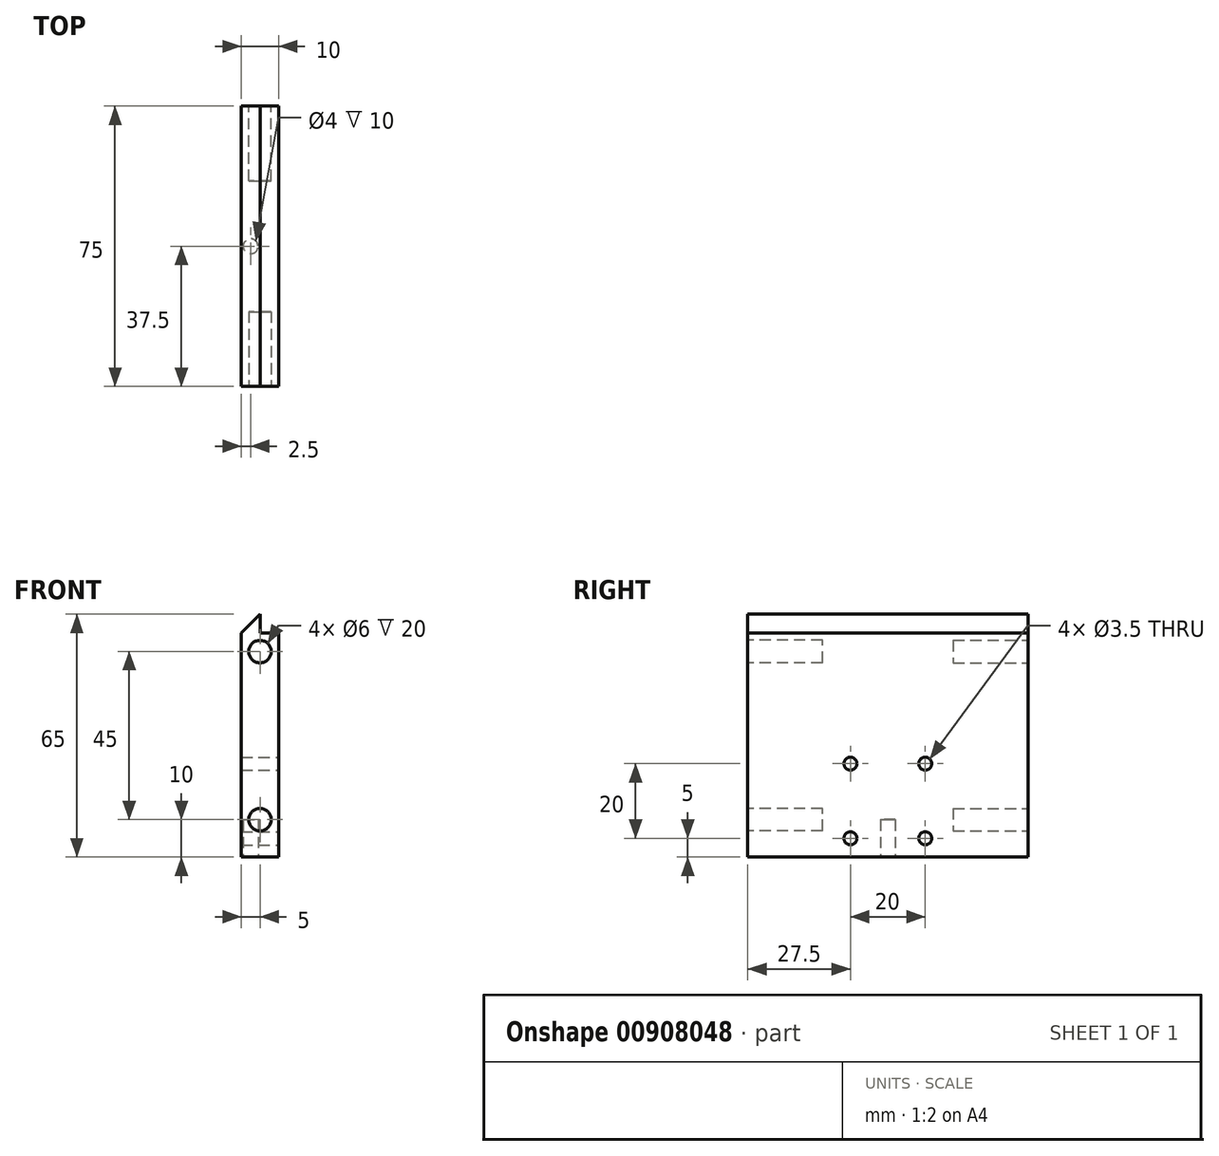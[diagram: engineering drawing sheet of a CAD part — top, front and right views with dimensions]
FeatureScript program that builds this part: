
annotation { "Feature Type Name" : "Feature", "Feature Type Description" : "" }
export const myFeature = defineFeature(function(context is Context, id is Id, definition is map)
    precondition{}
    {
        {
            var Q0;
            Q0=qCreatedBy(makeId("Front.planeOp"),FACE);
            var sketch = newSketch(context, id + "F0", { "sketchPlane" : qUnion([Q0])});
            skLineSegment(sketch, "E0.top", {"start": v(-5, -32.5) * mm, "end": v(5, -32.5) * mm});
            skLineSegment(sketch, "E0.left", {"start": v(-5, 27.5) * mm, "end": v(-5, -32.5) * mm});
            skLineSegment(sketch, "E0.right", {"start": v(5, 27.5) * mm, "end": v(5, -32.5) * mm});
            skPoint(sketch, "E0.middle", {"position": v(0, 0) * mm});
            skPoint(sketch, "E1", {"position": v(0, -22.5) * mm});
            skPoint(sketch, "E2", {"position": v(0, 22.5) * mm});
            skLineSegment(sketch, "E3", {"start": v(0, 32.5) * mm, "end": v(-5, 27.5) * mm});
            skLineSegment(sketch, "E4.top", {"start": v(0, 27.5) * mm, "end": v(5, 27.5) * mm});
            skLineSegment(sketch, "E4.left", {"start": v(0, 32.5) * mm, "end": v(0, 27.5) * mm});
            skSolve(sketch);
        }
        {
            var Q0;
            {var subQ1=sQuery(id+"F0.wireOp",EDGE,"E0.top");Q0=makeQuery(id+"F0.imprint","IMPRINT",FACE,{"disambiguationData":[TD([[makeQuery(id+"F0.imprint","IMPRINT",EDGE,{"derivedFrom":subQ1}),1.0]])]});}
            extrude(context, id + "F1", {"entities" : qUnion([Q0]), "depth" : 75 * mm, "offsetDistance" : 25 * mm});
        }
        {
            var Q0;
            Q0=makeQuery(id+"F1.opExtrude","SWEPT_FACE",FACE,{"disambiguationData":[OSD([sQuery(id+"F0.wireOp",EDGE,"E0.top")])]});
            var sketch = newSketch(context, id + "F2", { "sketchPlane" : qUnion([Q0])});
            skPoint(sketch, "E5.centerSnap0", {"position": v(-5, 37.5) * mm});
            skCircle(sketch, "E6", {"center": v(-2.5, 37.5) * mm, "radius": 2 * mm});
            skSolve(sketch);
        }
        {
            var Q0;
            Q0=makeQuery(id+"F1.opExtrude","SWEPT_FACE",FACE,{"disambiguationData":[OSD([sQuery(id+"F0.wireOp",EDGE,"E0.right")])]});
            var sketch = newSketch(context, id + "F3", { "sketchPlane" : qUnion([Q0])});
            skCircle(sketch, "E7", {"center": v(-27.5, -7.5) * mm, "radius": 1.75 * mm});
            skCircle(sketch, "E8", {"center": v(-47.5, -7.5) * mm, "radius": 1.75 * mm});
            skCircle(sketch, "E9", {"center": v(-27.5, -27.5) * mm, "radius": 1.75 * mm});
            skCircle(sketch, "E10", {"center": v(-47.5, -27.5) * mm, "radius": 1.75 * mm});
            skSolve(sketch);
        }
        {
            var Q0;
            Q0=qSketchRegion(id+"F3",true);
            extrude(context, id + "F4", {"entities" : qUnion([Q0]), "operationType" : NewBodyOperationType.REMOVE, "oppositeDirection" : true, "depth" : 25 * mm, "offsetDistance" : 25 * mm});
        }
        {
            var Q0;
            Q0=makeQuery(id+"F1.opExtrude","SWEPT_FACE",FACE,{"disambiguationData":[OSD([sQuery(id+"F0.wireOp",EDGE,"E0.top")])]});
            var sketch = newSketch(context, id + "F5", { "sketchPlane" : qUnion([Q0])});
            skSolve(sketch);
        }
        {
            var Q0;
            Q0=makeQuery(id+"F1.opExtrude","CAP_FACE",FACE,{"disambiguationData":[OSD([sQuery(id+"F0.wireOp",EDGE,"E0.top"),sQuery(id+"F0.wireOp",EDGE,"E0.left"),sQuery(id+"F0.wireOp",EDGE,"E0.right"),sQuery(id+"F0.wireOp",EDGE,"E3"),sQuery(id+"F0.wireOp",EDGE,"E4.top"),sQuery(id+"F0.wireOp",EDGE,"E4.left")])],"isStart":false});
            var sketch = newSketch(context, id + "F6", { "sketchPlane" : qUnion([Q0])});
            skCircle(sketch, "E11", {"center": v(0, -22.5) * mm, "radius": 3 * mm});
            skPoint(sketch, "E11.centerSnap0", {"position": v(0, -32.5) * mm});
            skSolve(sketch);
        }
        {
            var Q0;
            Q0=qSketchRegion(id+"F6",true);
            extrude(context, id + "F7", {"entities" : qUnion([Q0]), "operationType" : NewBodyOperationType.REMOVE, "oppositeDirection" : true, "depth" : 20 * mm, "offsetDistance" : 25 * mm});
        }
        {
            var Q0;
            Q0=makeQuery(id+"F1.opExtrude","CAP_FACE",FACE,{"disambiguationData":[OSD([sQuery(id+"F0.wireOp",EDGE,"E0.top"),sQuery(id+"F0.wireOp",EDGE,"E0.left"),sQuery(id+"F0.wireOp",EDGE,"E0.right"),sQuery(id+"F0.wireOp",EDGE,"E3"),sQuery(id+"F0.wireOp",EDGE,"E4.top"),sQuery(id+"F0.wireOp",EDGE,"E4.left")])],"isStart":false});
            var sketch = newSketch(context, id + "F8", { "sketchPlane" : qUnion([Q0])});
            skCircle(sketch, "E12", {"center": v(0, 22.5) * mm, "radius": 3 * mm});
            skSolve(sketch);
        }
        {
            var Q0;
            Q0=qSketchRegion(id+"F8",true);
            extrude(context, id + "F9", {"entities" : qUnion([Q0]), "operationType" : NewBodyOperationType.REMOVE, "oppositeDirection" : true, "depth" : 20 * mm, "offsetDistance" : 25 * mm});
        }
        {
            var Q0;
            Q0=makeQuery(id+"F1.opExtrude","CAP_FACE",FACE,{"disambiguationData":[OSD([sQuery(id+"F0.wireOp",EDGE,"E0.top"),sQuery(id+"F0.wireOp",EDGE,"E0.left"),sQuery(id+"F0.wireOp",EDGE,"E0.right"),sQuery(id+"F0.wireOp",EDGE,"E3"),sQuery(id+"F0.wireOp",EDGE,"E4.top"),sQuery(id+"F0.wireOp",EDGE,"E4.left")])],"isStart":true});
            var sketch = newSketch(context, id + "F10", { "sketchPlane" : qUnion([Q0])});
            skCircle(sketch, "E13", {"center": v(0, -22.5) * mm, "radius": 3 * mm});
            skPoint(sketch, "E13.centerSnap0", {"position": v(0, -32.5) * mm});
            skSolve(sketch);
        }
        {
            var Q0;
            Q0=qSketchRegion(id+"F10",true);
            extrude(context, id + "F11", {"entities" : qUnion([Q0]), "operationType" : NewBodyOperationType.REMOVE, "oppositeDirection" : true, "depth" : 20 * mm, "offsetDistance" : 25 * mm});
        }
        {
            var Q0;
            Q0=makeQuery(id+"F1.opExtrude","CAP_FACE",FACE,{"disambiguationData":[OSD([sQuery(id+"F0.wireOp",EDGE,"E0.top"),sQuery(id+"F0.wireOp",EDGE,"E0.left"),sQuery(id+"F0.wireOp",EDGE,"E0.right"),sQuery(id+"F0.wireOp",EDGE,"E3"),sQuery(id+"F0.wireOp",EDGE,"E4.top"),sQuery(id+"F0.wireOp",EDGE,"E4.left")])],"isStart":true});
            var sketch = newSketch(context, id + "F12", { "sketchPlane" : qUnion([Q0])});
            skCircle(sketch, "E14", {"center": v(0, 22.5) * mm, "radius": 3 * mm});
            skPoint(sketch, "E14.centerSnap0", {"position": v(0, -32.5) * mm});
            skSolve(sketch);
        }
        {
            var Q0;
            Q0=qSketchRegion(id+"F12",true);
            extrude(context, id + "F13", {"entities" : qUnion([Q0]), "operationType" : NewBodyOperationType.REMOVE, "oppositeDirection" : true, "depth" : 20 * mm, "offsetDistance" : 25 * mm});
        }
        {
            var Q0;
            Q0=qSketchRegion(id+"F2",true);
            extrude(context, id + "F14", {"entities" : qUnion([Q0]), "operationType" : NewBodyOperationType.REMOVE, "oppositeDirection" : true, "depth" : 10 * mm, "offsetDistance" : 25 * mm});
        }
        {
            var Q0;
            Q0=qSketchRegion(id+"F3",true);
            extrude(context, id + "F15", {"entities" : qUnion([Q0]), "operationType" : NewBodyOperationType.REMOVE, "oppositeDirection" : true, "depth" : 25 * mm, "offsetDistance" : 25 * mm});
        }
        {
            var Q0;
            Q0 = qSketchRegion(id + "F3", true);
            extrude(context, id + "F16", {"entities" : qUnion([Q0]), "operationType" : NewBodyOperationType.REMOVE, "oppositeDirection" : true, "depth" : 25 * mm, "offsetDistance" : 25 * mm});
        }
        {
            var Q0;
            Q0 = qSketchRegion(id + "F3", true);
            extrude(context, id + "F17", {"entities" : qUnion([Q0]), "operationType" : NewBodyOperationType.REMOVE, "oppositeDirection" : true, "depth" : 25 * mm, "offsetDistance" : 25 * mm});
        }
    });
